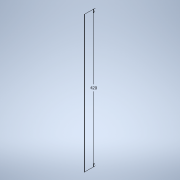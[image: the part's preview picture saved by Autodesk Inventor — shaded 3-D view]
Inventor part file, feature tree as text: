
AUTODESK INVENTOR PART (.ipt)
format: ipt  version: 2020 (Build 240168000, 168)  size: 83,456 bytes
history: native  units: in
note: dims shown in document units (in); Inventor stores cm internally (conversion verified against a paired STEP export)
features: sketch x1
ambient origin geometry x8: Origin, YZ Plane, XZ Plane, XY Plane, X Axis, Y Axis, Z Axis, Center Point
feature tree (1):
  sketch  "Sketch1"  dims[d0=16.5354in]
